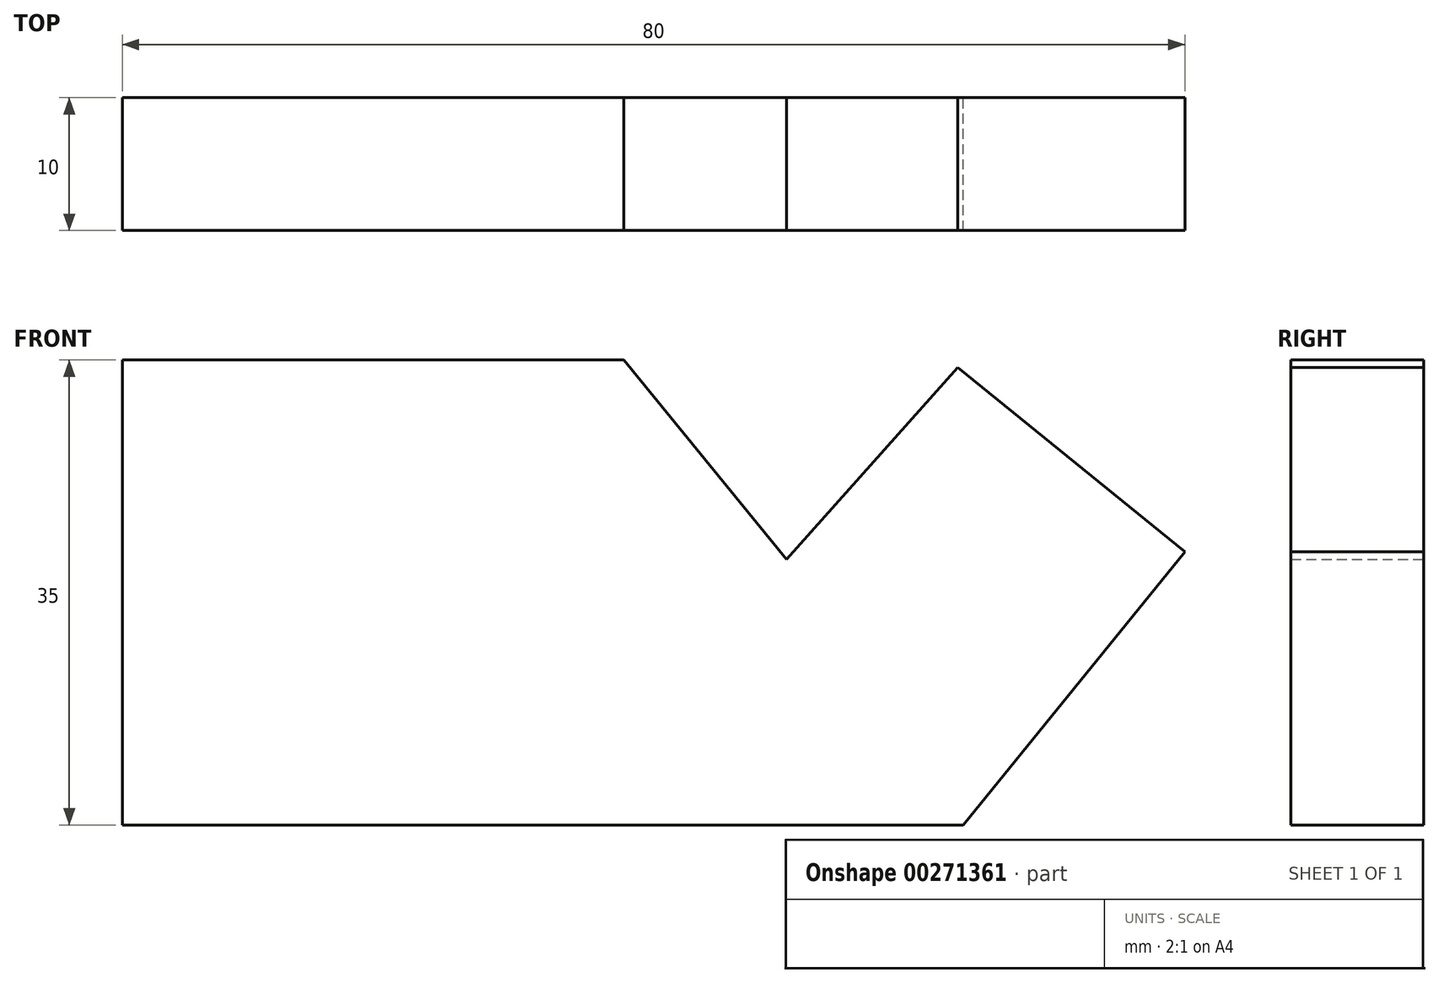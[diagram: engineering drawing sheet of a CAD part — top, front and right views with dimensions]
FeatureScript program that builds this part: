
annotation { "Feature Type Name" : "Feature", "Feature Type Description" : "" }
export const myFeature = defineFeature(function(context is Context, id is Id, definition is map)
    precondition{}
    {
        {
            var Q0;
            Q0=qCreatedBy(makeId("Front.planeOp"),FACE);
            var sketch = newSketch(context, id + "F0", { "sketchPlane" : qUnion([Q0])});
            skLineSegment(sketch, "E0.top", {"start": v(0, 35) * mm, "end": v(37.76, 35) * mm});
            skLineSegment(sketch, "E0.left", {"start": v(0, 0) * mm, "end": v(0, 35) * mm});
            skLineSegment(sketch, "E1", {"start": v(50, 20) * mm, "end": v(62.9, 34.44) * mm});
            skLineSegment(sketch, "E2", {"start": v(50, 20) * mm, "end": v(37.76, 35) * mm});
            skLineSegment(sketch, "E3", {"start": v(0, 0) * mm, "end": v(50, 0) * mm});
            skLineSegment(sketch, "E4", {"start": v(62.9, 34.44) * mm, "end": v(80, 20.56) * mm});
            skLineSegment(sketch, "E5", {"start": v(50, 0) * mm, "end": v(63.31, 0) * mm});
            skLineSegment(sketch, "E6", {"start": v(80, 20.56) * mm, "end": v(63.31, 0) * mm});
            skSolve(sketch);
        }
        {
            var Q0;
            Q0 = qSketchRegion(id + "F0", true);
            extrude(context, id + "F1", {"entities" : qUnion([Q0]), "depth" : 10 * mm});
        }
    });
